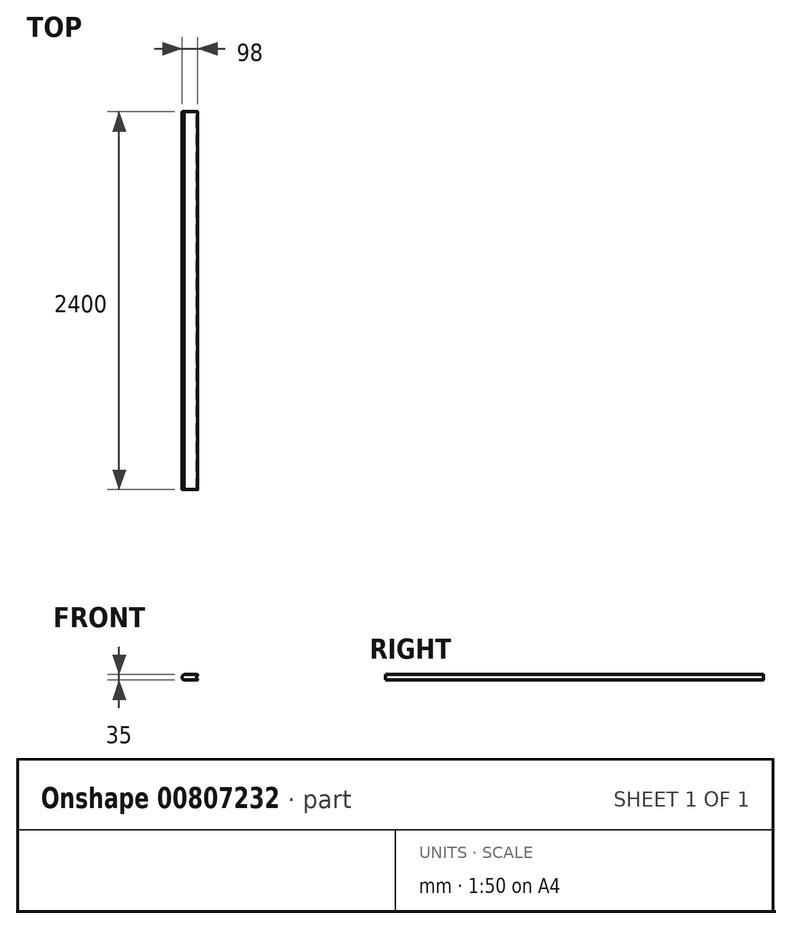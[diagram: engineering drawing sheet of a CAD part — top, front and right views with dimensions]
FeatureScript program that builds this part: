
annotation { "Feature Type Name" : "Feature", "Feature Type Description" : "" }
export const myFeature = defineFeature(function(context is Context, id is Id, definition is map)
    precondition{}
    {
        {
            var Q0;
            Q0=qCreatedBy(makeId("Front.planeOp"),FACE);
            var sketch = newSketch(context, id + "F0", { "sketchPlane" : qUnion([Q0])});
            skLineSegment(sketch, "E0.bottom", {"start": v(-50, 17.5) * mm, "end": v(50, 17.5) * mm});
            skLineSegment(sketch, "E0.top", {"start": v(-50, -17.5) * mm, "end": v(50, -17.5) * mm});
            skLineSegment(sketch, "E0.left", {"start": v(-50, 17.5) * mm, "end": v(-50, -17.5) * mm});
            skLineSegment(sketch, "E0.right", {"start": v(50, 17.5) * mm, "end": v(50, -17.5) * mm});
            skSolve(sketch);
        }
        {
            var Q0;
            Q0=makeQuery(id+"F0.imprint","IMPRINT",FACE,{"disambiguationData":[TD([[makeQuery(id+"F0.imprint","IMPRINT",EDGE,{"derivedFrom":sQuery(id+"F0.wireOp",EDGE,"E0.bottom")}),-1.0]])]});
            extrude(context, id + "F1", {"entities" : qUnion([Q0]), "depth" : 2400 * mm, "offsetDistance" : 25 * mm});
        }
        {
            var Q0;
            Q0=makeQuery(id+"F1.opExtrude","CAP_FACE",FACE,{"disambiguationData":[OSD([sQuery(id+"F0.wireOp",EDGE,"E0.bottom"),sQuery(id+"F0.wireOp",EDGE,"E0.top"),sQuery(id+"F0.wireOp",EDGE,"E0.left"),sQuery(id+"F0.wireOp",EDGE,"E0.right")])],"isStart":true});
            var sketch = newSketch(context, id + "F2", { "sketchPlane" : qUnion([Q0])});
            skArc(sketch, "E1", {"start": v(38.68, -17.5) * mm, "mid": v(49, 0) * mm, "end": v(38.68, 17.5) * mm});
            skLineSegment(sketch, "E2", {"start": v(38.68, 17.5) * mm, "end": v(50, 17.5) * mm});
            skLineSegment(sketch, "E3", {"start": v(50, 17.5) * mm, "end": v(50, -17.5) * mm});
            skLineSegment(sketch, "E4", {"start": v(50, -17.5) * mm, "end": v(38.68, -17.5) * mm});
            skLineSegment(sketch, "E5", {"start": v(0, 17.5) * mm, "end": v(-47, 17.5) * mm, "construction": true});
            skLineSegment(sketch, "E6", {"start": v(0, -17.5) * mm, "end": v(-47, -17.5) * mm, "construction": true});
            skArc(sketch, "E7", {"start": v(-48.42, -14.1) * mm, "mid": v(-42.61, 0) * mm, "end": v(-48.42, 14.1) * mm});
            skPoint(sketch, "E8.newPointA", {"position": v(-52.93, 17.5) * mm});
            skPoint(sketch, "E8.newPointB", {"position": v(-84.15, 17.5) * mm});
            skArc(sketch, "E8.filletArc", {"start": v(-47, 17.5) * mm, "mid": v(-48.85, 16.27) * mm, "end": v(-48.42, 14.1) * mm});
            skPoint(sketch, "E9.newPointB", {"position": v(-84.15, -17.5) * mm});
            skArc(sketch, "E9.filletArc", {"start": v(-48.42, -14.1) * mm, "mid": v(-48.85, -16.27) * mm, "end": v(-47, -17.5) * mm});
            skLineSegment(sketch, "E10", {"start": v(-47, 17.5) * mm, "end": v(-50, 17.5) * mm});
            skLineSegment(sketch, "E11", {"start": v(-50, 17.5) * mm, "end": v(-50, -17.5) * mm});
            skLineSegment(sketch, "E12", {"start": v(-50, -17.5) * mm, "end": v(-47, -17.5) * mm});
            skSolve(sketch);
        }
        {
            var Q0;
            Q0=makeQuery(id+"F2.imprint","IMPRINT",FACE,{"disambiguationData":[TD([[makeQuery(id+"F2.imprint","IMPRINT",EDGE,{"derivedFrom":sQuery(id+"F2.wireOp",EDGE,"E7")}),1.0]])]});
            var Q1;
            Q1=makeQuery(id+"F2.imprint","IMPRINT",FACE,{"disambiguationData":[TD([[makeQuery(id+"F2.imprint","IMPRINT",EDGE,{"derivedFrom":sQuery(id+"F2.wireOp",EDGE,"E1")}),-1.0]])]});
            extrude(context, id + "F3", {"entities" : qUnion([Q0, Q1]), "operationType" : NewBodyOperationType.REMOVE, "endBound" : BoundingType.UP_TO_NEXT, "oppositeDirection" : true, "depth" : 25 * mm, "offsetDistance" : 25 * mm});
        }
    });
